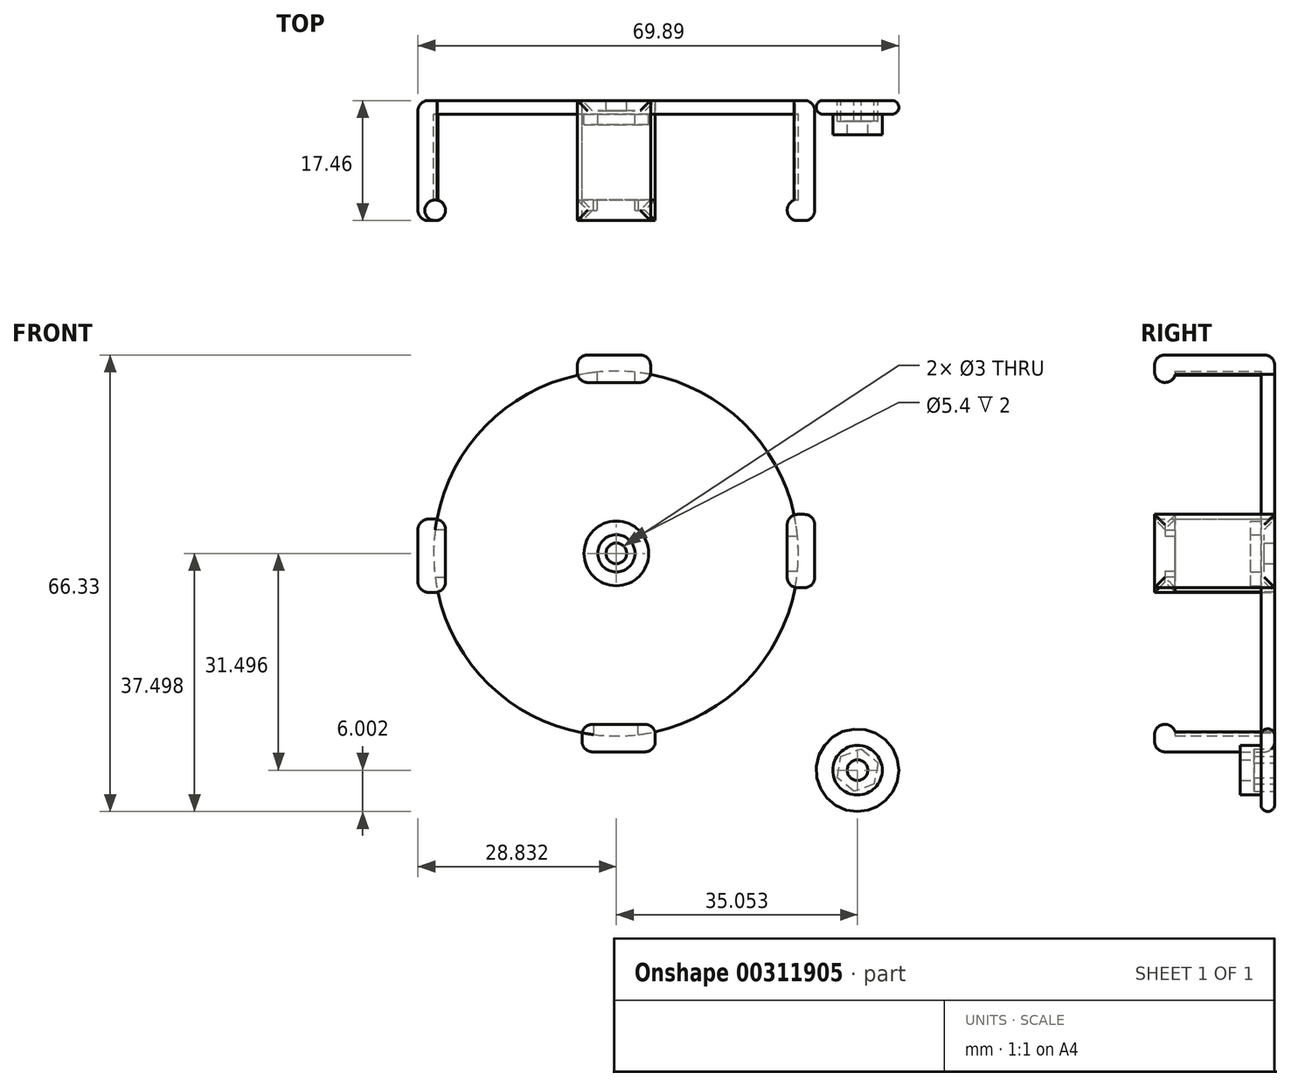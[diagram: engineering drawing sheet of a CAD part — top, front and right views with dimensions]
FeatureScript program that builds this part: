
annotation { "Feature Type Name" : "Feature", "Feature Type Description" : "" }
export const myFeature = defineFeature(function(context is Context, id is Id, definition is map)
    precondition{}
    {
        {
            var Q0;
            Q0=qCreatedBy(makeId("Front.planeOp"),FACE);
            var sketch = newSketch(context, id + "F0", { "sketchPlane" : qUnion([Q0])});
            skCircle(sketch, "E0", {"center": v(0, 0) * mm, "radius": 26.5 * mm});
            skLineSegment(sketch, "E1.bottom", {"start": v(25.88, 5.7) * mm, "end": v(28.88, 5.7) * mm});
            skLineSegment(sketch, "E1.top", {"start": v(25.88, -4.96) * mm, "end": v(28.88, -4.96) * mm});
            skLineSegment(sketch, "E1.left", {"start": v(25.88, 5.7) * mm, "end": v(25.88, -4.96) * mm});
            skLineSegment(sketch, "E1.right", {"start": v(28.88, 5.7) * mm, "end": v(28.88, -4.96) * mm});
            skLineSegment(sketch, "E2.1.0", {"start": v(-5.61, 28.86) * mm, "end": v(5.04, 28.86) * mm});
            skLineSegment(sketch, "E2.1.1", {"start": v(-5.61, 25.86) * mm, "end": v(-5.61, 28.86) * mm});
            skLineSegment(sketch, "E2.1.3", {"start": v(5.04, 25.86) * mm, "end": v(5.04, 28.86) * mm});
            skLineSegment(sketch, "E2.2.0", {"start": v(-28.78, -5.64) * mm, "end": v(-28.78, 5.01) * mm});
            skLineSegment(sketch, "E2.2.1", {"start": v(-25.78, -5.64) * mm, "end": v(-28.78, -5.64) * mm});
            skLineSegment(sketch, "E2.2.2", {"start": v(-25.78, -5.64) * mm, "end": v(-25.78, 5.01) * mm});
            skLineSegment(sketch, "E2.2.3", {"start": v(-25.78, 5.01) * mm, "end": v(-28.78, 5.01) * mm});
            skLineSegment(sketch, "E2.3.0", {"start": v(5.72, -28.8) * mm, "end": v(-4.93, -28.8) * mm});
            skLineSegment(sketch, "E2.3.1", {"start": v(5.72, -25.8) * mm, "end": v(5.72, -28.8) * mm});
            skLineSegment(sketch, "E2.3.2", {"start": v(5.72, -25.8) * mm, "end": v(-4.93, -25.8) * mm});
            skLineSegment(sketch, "E2.3.3", {"start": v(-4.93, -25.8) * mm, "end": v(-4.93, -28.8) * mm});
            skPoint(sketch, "E2.center", {"position": v(0.05, 0.03) * mm});
            skCircle(sketch, "E3", {"center": v(0.05, 0.03) * mm, "radius": 1.5 * mm});
            skCircle(sketch, "E4", {"center": v(0.05, 0.03) * mm, "radius": 2.7 * mm});
            skCircle(sketch, "E5", {"center": v(0.05, 0.03) * mm, "radius": 4.7 * mm});
            skCircle(sketch, "E6", {"center": v(35.1, -31.47) * mm, "radius": 6 * mm});
            skCircle(sketch, "E7", {"center": v(35.1, -31.47) * mm, "radius": 3.6 * mm});
            skCircle(sketch, "E8", {"center": v(35.1, -31.47) * mm, "radius": 1.5 * mm});
            skCircle(sketch, "E9.cCircle", {"center": v(35.1, -31.47) * mm, "radius": 2.72 * mm, "construction": true});
            skLineSegment(sketch, "E9.0", {"start": v(34.56, -34.56) * mm, "end": v(32.15, -32.54) * mm});
            skLineSegment(sketch, "E9.1", {"start": v(32.15, -32.54) * mm, "end": v(32.7, -29.45) * mm});
            skLineSegment(sketch, "E9.2", {"start": v(32.7, -29.45) * mm, "end": v(35.65, -28.38) * mm});
            skLineSegment(sketch, "E9.3", {"start": v(35.65, -28.38) * mm, "end": v(38.06, -30.4) * mm});
            skLineSegment(sketch, "E9.4", {"start": v(38.06, -30.4) * mm, "end": v(37.5, -33.49) * mm});
            skLineSegment(sketch, "E9.5", {"start": v(37.5, -33.49) * mm, "end": v(34.56, -34.56) * mm});
            skPoint(sketch, "E9.0.midPoint", {"position": v(33.36, -33.55) * mm});
            skSolve(sketch);
        }
        {
            var Q0;
            {var subQ1=sQuery(id+"F0.wireOp",EDGE,"E1.left");Q0=makeQuery(id+"F0.imprint","IMPRINT",FACE,{"disambiguationData":[TD([[makeQuery(id+"F0.imprint","IMPRINT",EDGE,{"derivedFrom":subQ1}),-1.0]])]});}
            var Q1;
            {var subQ0=sQuery(id+"F0.wireOp",EDGE,"134f1bf3-1e56-4d75-83fe-af74f4c24a06.2.1");Q1=makeQuery(id+"F0.imprint","IMPRINT",FACE,{"disambiguationData":[TD([[makeQuery(id+"F0.imprint","IMPRINT",EDGE,{"derivedFrom":subQ0}),-1.0]])]});}
            var Q2;
            {var subQ0=sQuery(id+"F0.wireOp",EDGE,"134f1bf3-1e56-4d75-83fe-af74f4c24a06.1.1");Q2=makeQuery(id+"F0.imprint","IMPRINT",FACE,{"disambiguationData":[TD([[makeQuery(id+"F0.imprint","IMPRINT",EDGE,{"derivedFrom":subQ0}),-1.0]])]});}
            var Q3;
            {var subQ0=sQuery(id+"F0.wireOp",EDGE,"E1.bottom");Q3=makeQuery(id+"F0.imprint","IMPRINT",FACE,{"disambiguationData":[TD([[makeQuery(id+"F0.imprint","IMPRINT",EDGE,{"derivedFrom":subQ0}),-1.0]])]});}
            var Q4;
            {var subQ0=sQuery(id+"F0.wireOp",EDGE,"134f1bf3-1e56-4d75-83fe-af74f4c24a06.2.2");Q4=makeQuery(id+"F0.imprint","IMPRINT",FACE,{"disambiguationData":[TD([[makeQuery(id+"F0.imprint","IMPRINT",EDGE,{"derivedFrom":subQ0}),1.0]])]});}
            var Q5;
            {var subQ0=sQuery(id+"F0.wireOp",EDGE,"134f1bf3-1e56-4d75-83fe-af74f4c24a06.3.2");Q5=makeQuery(id+"F0.imprint","IMPRINT",FACE,{"disambiguationData":[TD([[makeQuery(id+"F0.imprint","IMPRINT",EDGE,{"derivedFrom":subQ0}),1.0]])]});}
            var Q6;
            {var subQ4=sQuery(id+"F0.wireOp",EDGE,"134f1bf3-1e56-4d75-83fe-af74f4c24a06.3.1");Q6=makeQuery(id+"F0.imprint","IMPRINT",FACE,{"disambiguationData":[TD([[makeQuery(id+"F0.imprint","IMPRINT",EDGE,{"derivedFrom":subQ4}),-1.0]])]});}
            var Q7;
            {var subQ0=sQuery(id+"F0.wireOp",EDGE,"E1.left");Q7=makeQuery(id+"F0.imprint","IMPRINT",FACE,{"disambiguationData":[TD([[makeQuery(id+"F0.imprint","IMPRINT",EDGE,{"derivedFrom":subQ0}),1.0]])]});}
            var Q8;
            {var subQ0=sQuery(id+"F0.wireOp",EDGE,"134f1bf3-1e56-4d75-83fe-af74f4c24a06.1.2");Q8=makeQuery(id+"F0.imprint","IMPRINT",FACE,{"disambiguationData":[TD([[makeQuery(id+"F0.imprint","IMPRINT",EDGE,{"derivedFrom":subQ0}),1.0]])]});}
            var Q9;
            {var subQ4=sQuery(id+"F0.wireOp",EDGE,"E2.3.0");Q9=makeQuery(id+"F0.imprint","IMPRINT",FACE,{"disambiguationData":[TD([[makeQuery(id+"F0.imprint","IMPRINT",EDGE,{"derivedFrom":subQ4}),-1.0]])]});}
            var Q10;
            {var subQ0=sQuery(id+"F0.wireOp",EDGE,"E2.3.2");Q10=makeQuery(id+"F0.imprint","IMPRINT",FACE,{"disambiguationData":[TD([[makeQuery(id+"F0.imprint","IMPRINT",EDGE,{"derivedFrom":subQ0}),1.0]])]});}
            var Q11;
            {var subQ0=sQuery(id+"F0.wireOp",EDGE,"E2.1.2");Q11=makeQuery(id+"F0.imprint","IMPRINT",FACE,{"disambiguationData":[TD([[makeQuery(id+"F0.imprint","IMPRINT",EDGE,{"derivedFrom":subQ0}),1.0]])]});}
            var Q12;
            {var subQ4=sQuery(id+"F0.wireOp",EDGE,"E2.1.0");Q12=makeQuery(id+"F0.imprint","IMPRINT",FACE,{"disambiguationData":[TD([[makeQuery(id+"F0.imprint","IMPRINT",EDGE,{"derivedFrom":subQ4}),-1.0]])]});}
            var Q13;
            {var subQ0=sQuery(id+"F0.wireOp",EDGE,"E2.2.2");Q13=makeQuery(id+"F0.imprint","IMPRINT",FACE,{"disambiguationData":[TD([[makeQuery(id+"F0.imprint","IMPRINT",EDGE,{"derivedFrom":subQ0}),1.0]])]});}
            var Q14;
            {var subQ4=sQuery(id+"F0.wireOp",EDGE,"E2.2.0");Q14=makeQuery(id+"F0.imprint","IMPRINT",FACE,{"disambiguationData":[TD([[makeQuery(id+"F0.imprint","IMPRINT",EDGE,{"derivedFrom":subQ4}),-1.0]])]});}
            var Q15;
            Q15=makeQuery(id+"F0.imprint","IMPRINT",FACE,{"disambiguationData":[TD([[makeQuery(id+"F0.imprint","IMPRINT",EDGE,{"derivedFrom":sQuery(id+"F0.wireOp",EDGE,"rao16cFf-v3Dq-vnPg-bF51-cUyhHrZK7o5x")}),-1.0]])]});
            var Q16;
            Q16=makeQuery(id+"F0.imprint","IMPRINT",FACE,{"disambiguationData":[TD([[makeQuery(id+"F0.imprint","IMPRINT",EDGE,{"derivedFrom":sQuery(id+"F0.wireOp",EDGE,"rao16cFf-v3Dq-vnPg-bF51-cUyhHrZK7o5x")}),1.0]])]});
            var Q17;
            {var subQ0=sQuery(id+"F0.wireOp",EDGE,"E2.3.2");var subQ1=sQuery(id+"F0.wireOp",EDGE,"E0");var subQ2=makeQuery(id+"F0.imprint","INTERSECT",VERTEX,{"disambiguationData":[OD(0.0)],"derivedFrom":[subQ1,subQ0]});Q17=makeQuery(id+"F0.imprint","IMPRINT",FACE,{"disambiguationData":[TD([[makeQuery(id+"F0.imprint","IMPRINT",EDGE,{"disambiguationData":[TD([[subQ2,-1.0]])],"derivedFrom":subQ1}),1.0]])]});}
            var Q18;
            {var subQ0=sQuery(id+"F0.wireOp",EDGE,"E2.2.2");var subQ1=sQuery(id+"F0.wireOp",EDGE,"E0");var subQ2=makeQuery(id+"F0.imprint","INTERSECT",VERTEX,{"disambiguationData":[OD(0.0)],"derivedFrom":[subQ1,subQ0]});Q18=makeQuery(id+"F0.imprint","IMPRINT",FACE,{"disambiguationData":[TD([[makeQuery(id+"F0.imprint","IMPRINT",EDGE,{"disambiguationData":[TD([[subQ2,-1.0]])],"derivedFrom":subQ1}),1.0]])]});}
            var Q19;
            {var subQ0=sQuery(id+"F0.wireOp",EDGE,"E2.1.2");var subQ1=sQuery(id+"F0.wireOp",EDGE,"E0");var subQ2=makeQuery(id+"F0.imprint","INTERSECT",VERTEX,{"disambiguationData":[OD(0.0)],"derivedFrom":[subQ1,subQ0]});Q19=makeQuery(id+"F0.imprint","IMPRINT",FACE,{"disambiguationData":[TD([[makeQuery(id+"F0.imprint","IMPRINT",EDGE,{"disambiguationData":[TD([[subQ2,1.0]])],"derivedFrom":subQ1}),1.0]])]});}
            var Q20;
            Q20=makeQuery(id+"F0.imprint","IMPRINT",FACE,{"disambiguationData":[TD([[makeQuery(id+"F0.imprint","IMPRINT",EDGE,{"derivedFrom":sQuery(id+"F0.wireOp",EDGE,"E3")}),-1.0]])]});
            var Q21;
            Q21=makeQuery(id+"F0.imprint","IMPRINT",FACE,{"disambiguationData":[TD([[makeQuery(id+"F0.imprint","IMPRINT",EDGE,{"derivedFrom":sQuery(id+"F0.wireOp",EDGE,"E4")}),-1.0]])]});
            extrude(context, id + "F1", {"entities" : qUnion([Q0, Q1, Q2, Q3, Q4, Q5, Q6, Q7, Q8, Q9, Q10, Q11, Q12, Q13, Q14, Q15, Q16, Q17, Q18, Q19, Q20, Q21]), "depth" : 2 * mm});
        }
        {
            var Q0;
            Q0=makeQuery(id+"F0.imprint","IMPRINT",FACE,{"disambiguationData":[TD([[makeQuery(id+"F0.imprint","IMPRINT",EDGE,{"derivedFrom":sQuery(id+"F0.wireOp",EDGE,"E6")}),1.0]])]});
            extrude(context, id + "F2", {"entities" : qUnion([Q0]), "depth" : 2 * mm});
        }
        {
            var Q0;
            Q0=makeQuery(id+"F0.imprint","IMPRINT",FACE,{"disambiguationData":[TD([[makeQuery(id+"F0.imprint","IMPRINT",EDGE,{"derivedFrom":sQuery(id+"F0.wireOp",EDGE,"E7")}),1.0]])]});
            var Q1;
            Q1=makeQuery(id+"F0.imprint","IMPRINT",FACE,{"disambiguationData":[TD([[makeQuery(id+"F0.imprint","IMPRINT",EDGE,{"derivedFrom":sQuery(id+"F0.wireOp",EDGE,"E8")}),-1.0]])]});
            extrude(context, id + "F3", {"entities" : qUnion([Q0, Q1]), "operationType" : NewBodyOperationType.ADD, "depth" : 5 * mm});
        }
        {
            var Q0;
            Q0=makeQuery(id+"F0.imprint","IMPRINT",FACE,{"disambiguationData":[TD([[makeQuery(id+"F0.imprint","IMPRINT",EDGE,{"derivedFrom":sQuery(id+"F0.wireOp",EDGE,"E8")}),-1.0]])]});
            extrude(context, id + "F4", {"entities" : qUnion([Q0]), "operationType" : NewBodyOperationType.REMOVE, "depth" : 3 * mm});
        }
        {
            var Q0;
            Q0=makeQuery(id+"F0.imprint","IMPRINT",FACE,{"disambiguationData":[TD([[makeQuery(id+"F0.imprint","IMPRINT",EDGE,{"derivedFrom":sQuery(id+"F0.wireOp",EDGE,"E4")}),-1.0]])]});
            extrude(context, id + "F5", {"entities" : qUnion([Q0]), "operationType" : NewBodyOperationType.ADD, "depth" : 3.5 * mm});
        }
        {
            var Q0;
            {var subQ0=sQuery(id+"F0.wireOp",EDGE,"E3");Q0=makeQuery(id+"F5.boolean.opBoolean","SPLIT",FACE,{"disambiguationData":[TD([makeQuery(id+"F1.opExtrude","SWEPT_FACE",FACE,{"disambiguationData":[OSD([subQ0])]})])],"derivedFrom":makeQuery(id+"F1.opExtrude","CAP_FACE",FACE,{"disambiguationData":[OSD([sQuery(id+"F0.wireOp",EDGE,"E1.bottom"),sQuery(id+"F0.wireOp",EDGE,"E1.top"),sQuery(id+"F0.wireOp",EDGE,"E1.right"),sQuery(id+"F0.wireOp",EDGE,"E0"),sQuery(id+"F0.wireOp",EDGE,"E2.1.0"),sQuery(id+"F0.wireOp",EDGE,"E2.1.1"),sQuery(id+"F0.wireOp",EDGE,"E2.1.3"),sQuery(id+"F0.wireOp",EDGE,"E2.2.0"),sQuery(id+"F0.wireOp",EDGE,"E2.2.1"),sQuery(id+"F0.wireOp",EDGE,"E2.2.3"),sQuery(id+"F0.wireOp",EDGE,"E2.3.0"),sQuery(id+"F0.wireOp",EDGE,"E2.3.1"),sQuery(id+"F0.wireOp",EDGE,"E2.3.3"),subQ0])],"isStart":false})});}
            extrude(context, id + "F6", {"entities" : qUnion([Q0]), "operationType" : NewBodyOperationType.REMOVE, "oppositeDirection" : true, "depth" : .5 * mm});
        }
        {
            var Q0;
            {var subQ5=sQuery(id+"F0.wireOp",EDGE,"E2.1.0");Q0=makeQuery(id+"F0.imprint","IMPRINT",FACE,{"disambiguationData":[TD([[makeQuery(id+"F0.imprint","IMPRINT",EDGE,{"derivedFrom":subQ5}),-1.0]])]});}
            var Q1;
            {var subQ5=sQuery(id+"F0.wireOp",EDGE,"E2.2.0");Q1=makeQuery(id+"F0.imprint","IMPRINT",FACE,{"disambiguationData":[TD([[makeQuery(id+"F0.imprint","IMPRINT",EDGE,{"derivedFrom":subQ5}),-1.0]])]});}
            var Q2;
            {var subQ5=sQuery(id+"F0.wireOp",EDGE,"E2.3.0");Q2=makeQuery(id+"F0.imprint","IMPRINT",FACE,{"disambiguationData":[TD([[makeQuery(id+"F0.imprint","IMPRINT",EDGE,{"derivedFrom":subQ5}),-1.0]])]});}
            var Q3;
            {var subQ0=sQuery(id+"F0.wireOp",EDGE,"E1.bottom");Q3=makeQuery(id+"F0.imprint","IMPRINT",FACE,{"disambiguationData":[TD([[makeQuery(id+"F0.imprint","IMPRINT",EDGE,{"derivedFrom":subQ0}),-1.0]])]});}
            extrude(context, id + "F7", {"entities" : qUnion([Q0, Q1, Q2, Q3]), "operationType" : NewBodyOperationType.ADD, "depth" : 17.46 * mm});
        }
        {
            var Q0;
            {var subQ0=sQuery(id+"F0.wireOp",EDGE,"E2.2.0");Q0=makeQuery(id+"F7.boolean.opBoolean","MERGE",FACE,{"derivedFrom":[makeQuery(id+"F1.opExtrude","SWEPT_FACE",FACE,{"disambiguationData":[OSD([subQ0])]}),makeQuery(id+"F7.opExtrude","SWEPT_FACE",FACE,{"disambiguationData":[OSD([subQ0])]})]});}
            var sketch = newSketch(context, id + "F8", { "sketchPlane" : qUnion([Q0])});
            skLineSegment(sketch, "E10.bottom", {"start": v(17.46, 5.01) * mm, "end": v(14.46, 5.01) * mm});
            skLineSegment(sketch, "E10.top", {"start": v(17.46, -5.64) * mm, "end": v(14.46, -5.64) * mm});
            skLineSegment(sketch, "E10.left", {"start": v(17.46, 5.01) * mm, "end": v(17.46, -5.64) * mm});
            skLineSegment(sketch, "E10.right", {"start": v(14.46, 5.01) * mm, "end": v(14.46, -5.64) * mm});
            skSolve(sketch);
        }
        {
            var Q0;
            Q0=makeQuery(id+"F8.imprint","IMPRINT",FACE,{"disambiguationData":[TD([[makeQuery(id+"F8.imprint","IMPRINT",EDGE,{"derivedFrom":sQuery(id+"F8.wireOp",EDGE,"E10.bottom")}),1.0]])]});
            extrude(context, id + "F9", {"entities" : qUnion([Q0]), "operationType" : NewBodyOperationType.ADD, "oppositeDirection" : true, "depth" : 4 * mm});
        }
        {
            var Q0;
            Q0=makeQuery(id+"F9.opExtrude","CAP_FACE",FACE,{"disambiguationData":[OSD([sQuery(id+"F8.wireOp",EDGE,"E10.bottom"),sQuery(id+"F8.wireOp",EDGE,"E10.top"),sQuery(id+"F8.wireOp",EDGE,"E10.left"),sQuery(id+"F8.wireOp",EDGE,"E10.right")])],"isStart":false});
            var Q1;
            {var subQ0=sQuery(id+"F0.wireOp",EDGE,"E2.2.0");Q1=makeQuery(id+"F7.boolean.opBoolean","MERGE",FACE,{"derivedFrom":[makeQuery(id+"F1.opExtrude","SWEPT_FACE",FACE,{"disambiguationData":[OSD([subQ0])]}),makeQuery(id+"F7.opExtrude","SWEPT_FACE",FACE,{"disambiguationData":[OSD([subQ0])]})]});}
            fillet(context, id + "F10", {"entities" : qUnion([Q0, Q1]), "radius" : 1.5 * mm, "tangentPropagation" : true, "allowEdgeOverflow" : false});
        }
        {
            var Q0;
            {var subQ0=sQuery(id+"F0.wireOp",EDGE,"E2.3.0");Q0=makeQuery(id+"F7.boolean.opBoolean","MERGE",FACE,{"derivedFrom":[makeQuery(id+"F1.opExtrude","SWEPT_FACE",FACE,{"disambiguationData":[OSD([subQ0])]}),makeQuery(id+"F7.opExtrude","SWEPT_FACE",FACE,{"disambiguationData":[OSD([subQ0])]})]});}
            var sketch = newSketch(context, id + "F11", { "sketchPlane" : qUnion([Q0])});
            skLineSegment(sketch, "E11.bottom", {"start": v(-4.93, 17.46) * mm, "end": v(5.72, 17.46) * mm});
            skLineSegment(sketch, "E11.top", {"start": v(-4.93, 14.46) * mm, "end": v(5.72, 14.46) * mm});
            skLineSegment(sketch, "E11.left", {"start": v(-4.93, 17.46) * mm, "end": v(-4.93, 14.46) * mm});
            skLineSegment(sketch, "E11.right", {"start": v(5.72, 17.46) * mm, "end": v(5.72, 14.46) * mm});
            skSolve(sketch);
        }
        {
            var Q0;
            Q0=makeQuery(id+"F11.imprint","IMPRINT",FACE,{"disambiguationData":[TD([[makeQuery(id+"F11.imprint","IMPRINT",EDGE,{"derivedFrom":sQuery(id+"F11.wireOp",EDGE,"E11.bottom")}),1.0]])]});
            extrude(context, id + "F12", {"entities" : qUnion([Q0]), "operationType" : NewBodyOperationType.ADD, "oppositeDirection" : true, "depth" : 4 * mm});
        }
        {
            var Q0;
            {var subQ0=sQuery(id+"F0.wireOp",EDGE,"E2.3.0");Q0=makeQuery(id+"F7.boolean.opBoolean","MERGE",FACE,{"derivedFrom":[makeQuery(id+"F1.opExtrude","SWEPT_FACE",FACE,{"disambiguationData":[OSD([subQ0])]}),makeQuery(id+"F7.opExtrude","SWEPT_FACE",FACE,{"disambiguationData":[OSD([subQ0])]})]});}
            var Q1;
            Q1=makeQuery(id+"F12.opExtrude","CAP_FACE",FACE,{"disambiguationData":[OSD([sQuery(id+"F11.wireOp",EDGE,"E11.bottom"),sQuery(id+"F11.wireOp",EDGE,"E11.top"),sQuery(id+"F11.wireOp",EDGE,"E11.left"),sQuery(id+"F11.wireOp",EDGE,"E11.right")])],"isStart":false});
            fillet(context, id + "F13", {"entities" : qUnion([Q0, Q1]), "radius" : 1.5 * mm, "tangentPropagation" : true, "allowEdgeOverflow" : false});
        }
        {
            var Q0;
            Q0=makeQuery(id+"F2.opExtrude","CAP_EDGE",EDGE,{"disambiguationData":[OSD([sQuery(id+"F0.wireOp",EDGE,"E6")])],"isStart":true});
            var Q1;
            Q1=makeQuery(id+"F2.opExtrude","CAP_EDGE",EDGE,{"disambiguationData":[OSD([sQuery(id+"F0.wireOp",EDGE,"E6")])],"isStart":false});
            var Q2;
            Q2=makeQuery(id+"F2.opExtrude","CAP_EDGE",EDGE,{"disambiguationData":[OSD([sQuery(id+"F0.wireOp",EDGE,"E7")])],"isStart":false});
            fillet(context, id + "F14", {"entities" : qUnion([Q0, Q1, Q2]), "radius" : 1 * mm, "tangentPropagation" : true, "allowEdgeOverflow" : false});
        }
        {
            var Q0;
            {var subQ0=sQuery(id+"F0.wireOp",EDGE,"E2.1.0");Q0=makeQuery(id+"F7.boolean.opBoolean","MERGE",FACE,{"derivedFrom":[makeQuery(id+"F1.opExtrude","SWEPT_FACE",FACE,{"disambiguationData":[OSD([subQ0])]}),makeQuery(id+"F7.opExtrude","SWEPT_FACE",FACE,{"disambiguationData":[OSD([subQ0])]})]});}
            var sketch = newSketch(context, id + "F15", { "sketchPlane" : qUnion([Q0])});
            skLineSegment(sketch, "E12.bottom", {"start": v(5.04, -17.46) * mm, "end": v(-5.61, -17.46) * mm});
            skLineSegment(sketch, "E12.top", {"start": v(5.04, -14.46) * mm, "end": v(-5.61, -14.46) * mm});
            skLineSegment(sketch, "E12.left", {"start": v(5.04, -17.46) * mm, "end": v(5.04, -14.46) * mm});
            skLineSegment(sketch, "E12.right", {"start": v(-5.61, -17.46) * mm, "end": v(-5.61, -14.46) * mm});
            skSolve(sketch);
        }
        {
            var Q0;
            Q0=makeQuery(id+"F15.imprint","IMPRINT",FACE,{"disambiguationData":[TD([[makeQuery(id+"F15.imprint","IMPRINT",EDGE,{"derivedFrom":sQuery(id+"F15.wireOp",EDGE,"E12.bottom")}),1.0]])]});
            extrude(context, id + "F16", {"entities" : qUnion([Q0]), "operationType" : NewBodyOperationType.ADD, "oppositeDirection" : true, "depth" : 4 * mm});
        }
        {
            var Q0;
            {var subQ0=sQuery(id+"F0.wireOp",EDGE,"E2.1.0");Q0=makeQuery(id+"F7.boolean.opBoolean","MERGE",FACE,{"derivedFrom":[makeQuery(id+"F1.opExtrude","SWEPT_FACE",FACE,{"disambiguationData":[OSD([subQ0])]}),makeQuery(id+"F7.opExtrude","SWEPT_FACE",FACE,{"disambiguationData":[OSD([subQ0])]})]});}
            var Q1;
            Q1=makeQuery(id+"F16.opExtrude","CAP_FACE",FACE,{"disambiguationData":[OSD([sQuery(id+"F15.wireOp",EDGE,"E12.bottom"),sQuery(id+"F15.wireOp",EDGE,"E12.top"),sQuery(id+"F15.wireOp",EDGE,"E12.left"),sQuery(id+"F15.wireOp",EDGE,"E12.right")])],"isStart":false});
            fillet(context, id + "F17", {"entities" : qUnion([Q0, Q1]), "radius" : 1.5 * mm, "tangentPropagation" : true, "allowEdgeOverflow" : false});
        }
        {
            var Q0;
            {var subQ0=sQuery(id+"F0.wireOp",EDGE,"E1.right");Q0=makeQuery(id+"F7.boolean.opBoolean","MERGE",FACE,{"derivedFrom":[makeQuery(id+"F1.opExtrude","SWEPT_FACE",FACE,{"disambiguationData":[OSD([subQ0])]}),makeQuery(id+"F7.opExtrude","SWEPT_FACE",FACE,{"disambiguationData":[OSD([subQ0])]})]});}
            var sketch = newSketch(context, id + "F18", { "sketchPlane" : qUnion([Q0])});
            skLineSegment(sketch, "E13.bottom", {"start": v(-17.46, -4.96) * mm, "end": v(-14.46, -4.96) * mm});
            skLineSegment(sketch, "E13.top", {"start": v(-17.46, 5.7) * mm, "end": v(-14.46, 5.7) * mm});
            skLineSegment(sketch, "E13.left", {"start": v(-17.46, -4.96) * mm, "end": v(-17.46, 5.7) * mm});
            skLineSegment(sketch, "E13.right", {"start": v(-14.46, -4.96) * mm, "end": v(-14.46, 5.7) * mm});
            skSolve(sketch);
        }
        {
            var Q0;
            Q0=makeQuery(id+"F18.imprint","IMPRINT",FACE,{"disambiguationData":[TD([[makeQuery(id+"F18.imprint","IMPRINT",EDGE,{"derivedFrom":sQuery(id+"F18.wireOp",EDGE,"E13.bottom")}),1.0]])]});
            extrude(context, id + "F19", {"entities" : qUnion([Q0]), "operationType" : NewBodyOperationType.ADD, "oppositeDirection" : true, "depth" : 4 * mm});
        }
        {
            var Q0;
            {var subQ0=sQuery(id+"F0.wireOp",EDGE,"E1.right");Q0=makeQuery(id+"F7.boolean.opBoolean","MERGE",FACE,{"derivedFrom":[makeQuery(id+"F1.opExtrude","SWEPT_FACE",FACE,{"disambiguationData":[OSD([subQ0])]}),makeQuery(id+"F7.opExtrude","SWEPT_FACE",FACE,{"disambiguationData":[OSD([subQ0])]})]});}
            var Q1;
            Q1=makeQuery(id+"F19.opExtrude","CAP_FACE",FACE,{"disambiguationData":[OSD([sQuery(id+"F18.wireOp",EDGE,"E13.bottom"),sQuery(id+"F18.wireOp",EDGE,"E13.top"),sQuery(id+"F18.wireOp",EDGE,"E13.left"),sQuery(id+"F18.wireOp",EDGE,"E13.right")])],"isStart":false});
            fillet(context, id + "F20", {"entities" : qUnion([Q0, Q1]), "radius" : 1.5 * mm, "tangentPropagation" : true, "allowEdgeOverflow" : false});
        }
    });
